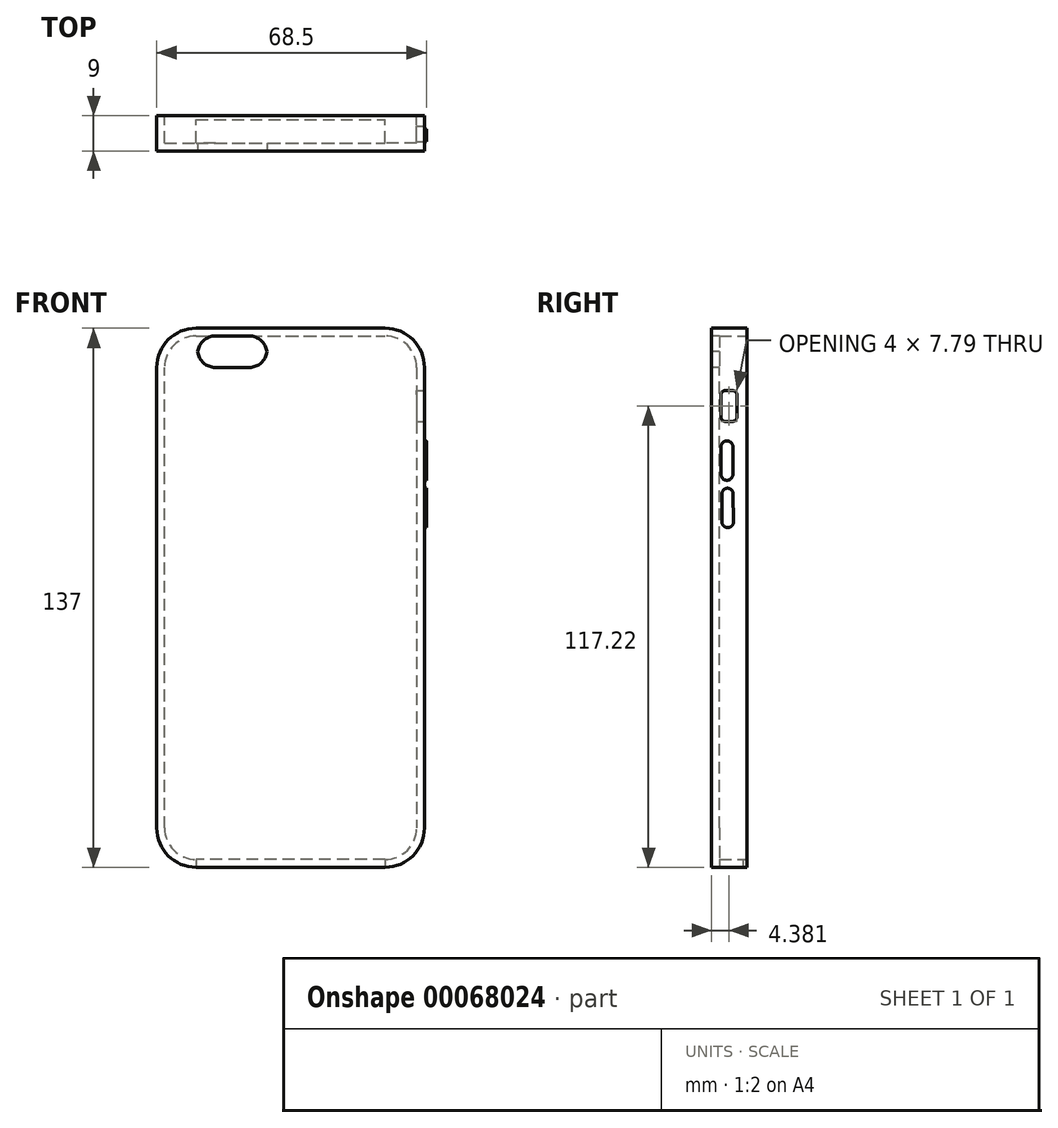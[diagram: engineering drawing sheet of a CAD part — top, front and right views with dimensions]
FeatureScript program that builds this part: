
annotation { "Feature Type Name" : "Feature", "Feature Type Description" : "" }
export const myFeature = defineFeature(function(context is Context, id is Id, definition is map)
    precondition{}
    {
        {
            var Q0;
            Q0=qCreatedBy(makeId("Front.planeOp"),FACE);
            var sketch = newSketch(context, id + "F0", { "sketchPlane" : qUnion([Q0])});
            skLineSegment(sketch, "E0", {"start": v(20.54, 71.36) * mm, "end": v(20.54, -45.64) * mm});
            skLineSegment(sketch, "E1", {"start": v(10.54, -55.64) * mm, "end": v(-37.46, -55.64) * mm});
            skLineSegment(sketch, "E2", {"start": v(-47.46, -45.64) * mm, "end": v(-47.46, 71.36) * mm});
            skLineSegment(sketch, "E3", {"start": v(-37.46, 81.36) * mm, "end": v(10.54, 81.36) * mm});
            skPoint(sketch, "E4.visualSharp", {"position": v(-47.46, 81.36) * mm});
            skArc(sketch, "E4.filletArc", {"start": v(-37.46, 81.36) * mm, "mid": v(-44.53, 78.43) * mm, "end": v(-47.46, 71.36) * mm});
            skPoint(sketch, "E5.visualSharp", {"position": v(20.54, 81.36) * mm});
            skArc(sketch, "E5.filletArc", {"start": v(20.54, 71.36) * mm, "mid": v(17.6, 78.43) * mm, "end": v(10.54, 81.36) * mm});
            skPoint(sketch, "E6.visualSharp", {"position": v(20.54, -55.64) * mm});
            skArc(sketch, "E6.filletArc", {"start": v(10.54, -55.64) * mm, "mid": v(17.6, -52.7) * mm, "end": v(20.54, -45.64) * mm});
            skPoint(sketch, "E7.visualSharp", {"position": v(-47.46, -55.64) * mm});
            skArc(sketch, "E7.filletArc", {"start": v(-47.46, -45.64) * mm, "mid": v(-44.53, -52.7) * mm, "end": v(-37.46, -55.64) * mm});
            skSolve(sketch);
        }
        {
            var Q0;
            Q0 = qSketchRegion(id + "F0", true);
            extrude(context, id + "F1", {"entities" : qUnion([Q0]), "depth" : 9 * mm});
        }
        {
            var Q0;
            Q0=makeQuery(id+"F1.opExtrude","CAP_FACE",FACE,{"disambiguationData":[OSD([sQuery(id+"F0.wireOp",EDGE,"E0"),sQuery(id+"F0.wireOp",EDGE,"E1"),sQuery(id+"F0.wireOp",EDGE,"E2"),sQuery(id+"F0.wireOp",EDGE,"E3")])],"isStart":true});
            shell(context, id + "F2", {"entities" : qUnion([Q0]), "thickness" : 2 * mm});
        }
        {
            var Q0;
            Q0=makeQuery(id+"F1.opExtrude","CAP_FACE",FACE,{"disambiguationData":[OSD([sQuery(id+"F0.wireOp",EDGE,"E0"),sQuery(id+"F0.wireOp",EDGE,"E1"),sQuery(id+"F0.wireOp",EDGE,"E2"),sQuery(id+"F0.wireOp",EDGE,"E3"),sQuery(id+"F0.wireOp",EDGE,"E4.filletArc"),sQuery(id+"F0.wireOp",EDGE,"E5.filletArc"),sQuery(id+"F0.wireOp",EDGE,"E6.filletArc"),sQuery(id+"F0.wireOp",EDGE,"E7.filletArc")])],"isStart":false});
            var sketch = newSketch(context, id + "F3", { "sketchPlane" : qUnion([Q0])});
            skLineSegment(sketch, "E8", {"start": v(-47.46, 71.36) * mm, "end": v(-37.06, 71.36) * mm});
            skLineSegment(sketch, "E9", {"start": v(-37.06, 71.36) * mm, "end": v(-47.06, 71.45) * mm});
            skLineSegment(sketch, "E10", {"start": v(-47.06, 71.45) * mm, "end": v(-37.06, 71.36) * mm});
            skLineSegment(sketch, "E11", {"start": v(20.54, 71.36) * mm, "end": v(-19.46, 71.36) * mm});
            skLineSegment(sketch, "E12", {"start": v(-32.56, 71.36) * mm, "end": v(-23.96, 71.36) * mm});
            skLineSegment(sketch, "E13", {"start": v(-37.06, 71.36) * mm, "end": v(-37.06, 79.36) * mm});
            skLineSegment(sketch, "E14", {"start": v(-37.06, 75.86) * mm, "end": v(-37.06, 74.86) * mm});
            skLineSegment(sketch, "E15", {"start": v(-19.46, 74.86) * mm, "end": v(-19.46, 75.86) * mm});
            skLineSegment(sketch, "E16", {"start": v(-23.96, 79.36) * mm, "end": v(-32.56, 79.36) * mm});
            skPoint(sketch, "E17.visualSharp", {"position": v(-37.06, 71.36) * mm});
            skArc(sketch, "E17.filletArc", {"start": v(-37.06, 75.86) * mm, "mid": v(-35.75, 72.68) * mm, "end": v(-32.56, 71.36) * mm});
            skPoint(sketch, "E18.visualSharp", {"position": v(-37.06, 79.36) * mm});
            skArc(sketch, "E18.filletArc", {"start": v(-32.56, 79.36) * mm, "mid": v(-35.75, 78.04) * mm, "end": v(-37.06, 74.86) * mm});
            skPoint(sketch, "E19.visualSharp", {"position": v(-19.46, 71.36) * mm});
            skArc(sketch, "E19.filletArc", {"start": v(-23.96, 71.36) * mm, "mid": v(-20.78, 72.68) * mm, "end": v(-19.46, 75.86) * mm});
            skPoint(sketch, "E20.visualSharp", {"position": v(-19.46, 79.36) * mm});
            skArc(sketch, "E20.filletArc", {"start": v(-19.46, 74.86) * mm, "mid": v(-20.78, 78.04) * mm, "end": v(-23.96, 79.36) * mm});
            skSolve(sketch);
        }
        {
            var Q0;
            {var subQ1=sQuery(id+"F3.wireOp",EDGE,"E12");Q0=makeQuery(id+"F3.imprint","IMPRINT",FACE,{"disambiguationData":[TD([[makeQuery(id+"F3.imprint","IMPRINT",EDGE,{"derivedFrom":subQ1}),1.0]])]});}
            extrude(context, id + "F4", {"entities" : qUnion([Q0]), "operationType" : NewBodyOperationType.REMOVE, "endBound" : BoundingType.THROUGH_ALL, "oppositeDirection" : true, "depth" : 25 * mm});
        }
        {
            var Q0;
            Q0=makeQuery(id+"F1.opExtrude","SWEPT_FACE",FACE,{"disambiguationData":[OSD([sQuery(id+"F0.wireOp",EDGE,"E1")])]});
            var sketch = newSketch(context, id + "F5", { "sketchPlane" : qUnion([Q0])});
            skLineSegment(sketch, "E21", {"start": v(-32.64, 9) * mm, "end": v(-32.64, 8) * mm});
            skLineSegment(sketch, "E22", {"start": v(-32.64, 8) * mm, "end": v(-32.64, 9) * mm});
            skLineSegment(sketch, "E23", {"start": v(-32.58, 0) * mm, "end": v(-32.58, 1) * mm});
            skLineSegment(sketch, "E24", {"start": v(-32.58, 1) * mm, "end": v(-32.58, 0) * mm});
            skLineSegment(sketch, "E25", {"start": v(-37.46, 1) * mm, "end": v(10.54, 1) * mm});
            skLineSegment(sketch, "E26", {"start": v(-37.46, 8) * mm, "end": v(10.54, 8) * mm});
            skLineSegment(sketch, "E27", {"start": v(10.54, 8) * mm, "end": v(10.54, 1) * mm});
            skLineSegment(sketch, "E28", {"start": v(-37.46, 1) * mm, "end": v(-37.46, 8) * mm});
            skSolve(sketch);
        }
        {
            var Q0;
            Q0 = qSketchRegion(id + "F5", true);
            extrude(context, id + "F6", {"entities" : qUnion([Q0]), "operationType" : NewBodyOperationType.REMOVE, "depth" : 25 * mm});
        }
        {
            var Q0;
            Q0 = qSketchRegion(id + "F5", true);
            extrude(context, id + "F7", {"entities" : qUnion([Q0]), "operationType" : NewBodyOperationType.REMOVE, "oppositeDirection" : true, "depth" : 25 * mm});
        }
        {
            var Q0;
            Q0=makeQuery(id+"F7.boolean.opBoolean","COPY",FACE,{"derivedFrom":makeQuery(id+"F7.opExtrude","SWEPT_FACE",FACE,{"disambiguationData":[OSD([sQuery(id+"F5.wireOp",EDGE,"E26")])]})});
            extrude(context, id + "F8", {"entities" : qUnion([Q0]), "operationType" : NewBodyOperationType.ADD, "depth" : 1 * mm});
        }
        {
            var Q0;
            Q0=makeQuery(id+"F1.opExtrude","SWEPT_FACE",FACE,{"disambiguationData":[OSD([sQuery(id+"F0.wireOp",EDGE,"E0")])]});
            var sketch = newSketch(context, id + "F9", { "sketchPlane" : qUnion([Q0])});
            skLineSegment(sketch, "E29", {"start": v(-4.62, 57.68) * mm, "end": v(-5.62, 57.68) * mm});
            skLineSegment(sketch, "E30", {"start": v(-4.62, 57.68) * mm, "end": v(-3.62, 57.68) * mm});
            skLineSegment(sketch, "E31", {"start": v(-6.62, 58.68) * mm, "end": v(-6.62, 64.48) * mm});
            skLineSegment(sketch, "E32", {"start": v(-5.62, 65.48) * mm, "end": v(-4.62, 65.48) * mm});
            skLineSegment(sketch, "E33", {"start": v(-3.62, 65.48) * mm, "end": v(-4.62, 65.48) * mm});
            skLineSegment(sketch, "E34", {"start": v(-2.62, 64.48) * mm, "end": v(-2.62, 58.68) * mm});
            skPoint(sketch, "E35.visualSharp", {"position": v(-6.62, 57.68) * mm});
            skArc(sketch, "E35.filletArc", {"start": v(-6.62, 58.68) * mm, "mid": v(-6.33, 57.98) * mm, "end": v(-5.62, 57.68) * mm});
            skPoint(sketch, "E36.visualSharp", {"position": v(-2.62, 57.68) * mm});
            skArc(sketch, "E36.filletArc", {"start": v(-3.62, 57.68) * mm, "mid": v(-2.91, 57.98) * mm, "end": v(-2.62, 58.68) * mm});
            skPoint(sketch, "E37.visualSharp", {"position": v(-2.62, 65.48) * mm});
            skArc(sketch, "E37.filletArc", {"start": v(-2.62, 64.48) * mm, "mid": v(-2.91, 65.18) * mm, "end": v(-3.62, 65.48) * mm});
            skPoint(sketch, "E38.visualSharp", {"position": v(-6.62, 65.48) * mm});
            skArc(sketch, "E38.filletArc", {"start": v(-5.62, 65.48) * mm, "mid": v(-6.33, 65.18) * mm, "end": v(-6.62, 64.48) * mm});
            skSolve(sketch);
        }
        {
            var Q0;
            Q0 = qSketchRegion(id + "F9", true);
            extrude(context, id + "F10", {"entities" : qUnion([Q0]), "operationType" : NewBodyOperationType.REMOVE, "oppositeDirection" : true, "depth" : 25 * mm});
        }
        {
            var Q0;
            Q0=makeQuery(id+"F1.opExtrude","SWEPT_FACE",FACE,{"disambiguationData":[OSD([sQuery(id+"F0.wireOp",EDGE,"E0")])]});
            var sketch = newSketch(context, id + "F11", { "sketchPlane" : qUnion([Q0])});
            skLineSegment(sketch, "E39", {"start": v(-6.62, 57.68) * mm, "end": v(-6.62, 52.68) * mm});
            skLineSegment(sketch, "E40", {"start": v(-5.12, 52.68) * mm, "end": v(-5.12, 52.68) * mm});
            skLineSegment(sketch, "E41", {"start": v(-3.62, 52.68) * mm, "end": v(-3.62, 42.68) * mm});
            skLineSegment(sketch, "E42", {"start": v(-3.62, 44.18) * mm, "end": v(-3.62, 51.18) * mm});
            skLineSegment(sketch, "E43", {"start": v(-6.62, 51.18) * mm, "end": v(-6.62, 44.18) * mm});
            skLineSegment(sketch, "E44", {"start": v(-5.12, 42.68) * mm, "end": v(-5.12, 42.68) * mm});
            skPoint(sketch, "E45.visualSharp", {"position": v(-6.62, 42.68) * mm});
            skArc(sketch, "E45.filletArc", {"start": v(-6.62, 44.18) * mm, "mid": v(-6.18, 43.12) * mm, "end": v(-5.12, 42.68) * mm});
            skPoint(sketch, "E46.visualSharp", {"position": v(-6.62, 52.68) * mm});
            skArc(sketch, "E46.filletArc", {"start": v(-5.12, 52.68) * mm, "mid": v(-6.18, 52.24) * mm, "end": v(-6.62, 51.18) * mm});
            skPoint(sketch, "E47.visualSharp", {"position": v(-3.62, 52.68) * mm});
            skArc(sketch, "E47.filletArc", {"start": v(-3.62, 51.18) * mm, "mid": v(-4.06, 52.24) * mm, "end": v(-5.12, 52.68) * mm});
            skPoint(sketch, "E48.visualSharp", {"position": v(-3.62, 42.68) * mm});
            skArc(sketch, "E48.filletArc", {"start": v(-5.12, 42.68) * mm, "mid": v(-4.06, 43.12) * mm, "end": v(-3.62, 44.18) * mm});
            skSolve(sketch);
        }
        {
            var Q0;
            Q0 = qSketchRegion(id + "F11", true);
            var Q1;
            Q1=makeQuery(id+"F11.imprint","IMPRINT",FACE,{"disambiguationData":[TD([[makeQuery(id+"F11.imprint","IMPRINT",EDGE,{"derivedFrom":sQuery(id+"F11.wireOp",EDGE,"E42")}),1.0]])]});
            extrude(context, id + "F12", {"entities" : qUnion([Q0, Q1]), "operationType" : NewBodyOperationType.ADD, "depth" : 0.5 * mm});
        }
        {
            var Q0;
            Q0=makeQuery(id+"F1.opExtrude","SWEPT_FACE",FACE,{"disambiguationData":[OSD([sQuery(id+"F0.wireOp",EDGE,"E0")])]});
            var sketch = newSketch(context, id + "F13", { "sketchPlane" : qUnion([Q0])});
            skLineSegment(sketch, "E49", {"start": v(-5.12, 42.68) * mm, "end": v(-6.4, 42.68) * mm});
            skLineSegment(sketch, "E50", {"start": v(-6.4, 32.18) * mm, "end": v(-6.4, 39.2) * mm});
            skLineSegment(sketch, "E51", {"start": v(-4.9, 30.68) * mm, "end": v(-4.93, 30.68) * mm});
            skLineSegment(sketch, "E52", {"start": v(-3.43, 32.2) * mm, "end": v(-3.54, 39.23) * mm});
            skLineSegment(sketch, "E53", {"start": v(-3.61, 42.68) * mm, "end": v(-6.4, 42.68) * mm});
            skArc(sketch, "E54.filletArc", {"start": v(-6.4, 32.18) * mm, "mid": v(-5.96, 31.12) * mm, "end": v(-4.9, 30.68) * mm});
            skLineSegment(sketch, "E55", {"start": v(-5.06, 40.7) * mm, "end": v(-4.93, 40.7) * mm});
            skPoint(sketch, "E56.visualSharp", {"position": v(-6.4, 40.68) * mm});
            skArc(sketch, "E56.filletArc", {"start": v(-4.93, 40.7) * mm, "mid": v(-5.97, 40.26) * mm, "end": v(-6.4, 39.2) * mm});
            skPoint(sketch, "E57.newPointA", {"position": v(-3.6, 42.68) * mm});
            skArc(sketch, "E57.filletArc", {"start": v(-3.54, 39.23) * mm, "mid": v(-4, 40.28) * mm, "end": v(-5.06, 40.7) * mm});
            skPoint(sketch, "E58.visualSharp", {"position": v(-3.4, 30.68) * mm});
            skArc(sketch, "E58.filletArc", {"start": v(-4.93, 30.68) * mm, "mid": v(-3.86, 31.13) * mm, "end": v(-3.43, 32.2) * mm});
            skSolve(sketch);
        }
        {
            var Q0;
            Q0 = qSketchRegion(id + "F13", true);
            extrude(context, id + "F14", {"entities" : qUnion([Q0]), "depth" : 0.5 * mm});
        }
    });
